# Revit family: Sanitary_Showers_hansgrohe_26243XXX-Rainfinity-Shoulder-shower-500_NEW
name_source: partatom
category: Plumbing Fixtures
revit_build: Autodesk Revit 2018 (Build: 20170223_1515(x64)
units: mm (PartAtom-declared; Revit-internal decimal feet)

## family parameters
Always vertical = No
Cut with Voids When Loaded = No
OmniClass Number = 23.31.17.00
OmniClass Title = Showers
Part Type = Normal
Room Calculation Point = No
Round Connector Dimension = Use Diameter
Shared = No
Work Plane-Based = Yes

## types (6) — shared parameters
Always visible = Yes
BIMobject category = Showers
Connector Description = Water Inlet 12.7mm
Default Elevation = 1219.2 mm  [stored 4 ft]
Description = Rainfinity Shoulder shower 500 1jet with shower shelf
Diameter = 13 mm
Edition number = 1
IFC Classification = Sanitary Terminal
Manufacturer = Hansgrohe
Manufacturer name = hansgrohe
Material 2 = Hansgrohe - Plastic - Graphite
Model = 26243XXX
OmniClass Code = 23-31 17 00
OmniClass Description = Showers
Product Guid = f2f25f9e-4b13-4861-938d-1f3c05201139
Product SKU = 26243XXX
Product data url = https://bimobject.com
Product family = Rainfinity
Product group = Body showers
Product name = 26243XXX Rainfinity Shoulder shower 500 1jet with shower shelf
Product url = https://www.hansgrohe.com
QR code = https://bimobject.com
URL = https://www.hansgrohe.com
Weight Net (Kg) = 2,3

## per-type parameters (varying)
| type | Material 1 | Material 3 |
| 990 Polished Gold Optic | Hansgrohe - Metal - 990 Polished Gold Optic | Hansgrohe - Plastic - Graphite |
| 700 Matt White | Hansgrohe - Metal - 700 Matt White | Hansgrohe - Plastic - Graphite |
| 670 Matt Black | Hansgrohe - Metal - 670 Matt Black | Hansgrohe - Plastic - Graphite |
| 340 Brushed Black Chrome | Hansgrohe - Metal - 340 Brushed Black Chrome | Hansgrohe - Plastic - Graphite |
| 140 Brushed Bronze | Hansgrohe - Metal - 140 Brushed Bronze | Hansgrohe - Plastic - Graphite |
| 000 Chrome | Hansgrohe - Metal - 000 Chrome | Hansgrohe - Glass - Mirror glass |

note: [stored X ft] marks values corroborated as IEEE doubles in the binary element streams (Revit-internal decimal feet)

## geometry (parser evidence)
native form markers: Sweep x2
no freeform markers — native parametric forms only
